# Revit family: CONTURA II COMPACT TWIN SHOWER
name_source: partatom
category: Plumbing Fixtures
units: mm (PartAtom-declared; Revit-internal decimal feet)

## family parameters
Cut with Voids When Loaded = No
Host = Face
OmniClass Number = 23.45.05.14.17
OmniClass Title = Showers
Part Type = Normal
Room Calculation Point = No
Round Connector Dimension = Use Diameter
Shared = No

## types (5) — shared parameters
CW Connection = Yes
HW Connection = Yes
Manufacturer = GWA Bathrooms & Kitchens
Material_Sprays = GWA-Plastic-General
URL = https://www.caroma.com.au
Vent Connection = No
Waste Connection = No
zero-valued in all types: Default Elevation

## per-type parameters (varying)
| type | Material | Material_Face | Model |
| CONTURA II COMPACT TWIN SHOWER - CHROME | GWA_Metal-Chrome | GWA_Metal-Chrome | 849082C43A |
| CONTURA II COMPACT TWIN SHOWER - MATTE BLACK | GWA-Metal-Black | GWA-Metal-Black | 849082B43A |
| CONTURA II COMPACT TWIN SHOWER - BRUSHED BRASS | GWA_Metal-Brushed-Brass | GWA_Metal-Brushed-Brass | 849082BB43A |
| CONTURA II COMPACT TWIN SHOWER - BRUSHED BRONZE | GWA_Metal-Brushed-Bronze | GWA_Metal-Brushed-Bronze | 849082BBZ43A |
| CONTURA II COMPACT TWIN SHOWER - BRUSHED NICKEL | GWA_Metal-Brushed-Nickel | GWA_Metal-Brushed-Nickel | 849082BN43A |

note: column(s) folded — value = type name in every type: Description

## geometry (parser evidence)
native form markers: Blend x2, Sweep x8
no freeform markers — native parametric forms only
